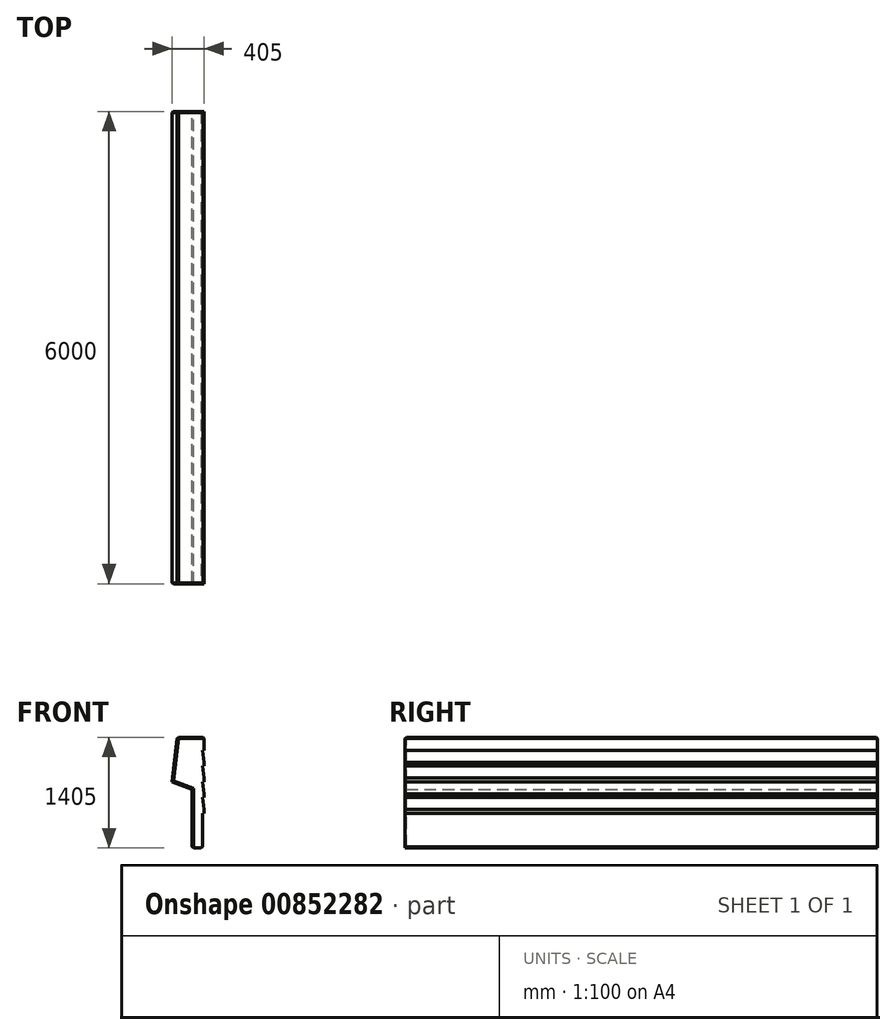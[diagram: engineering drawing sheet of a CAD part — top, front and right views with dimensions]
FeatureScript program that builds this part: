
annotation { "Feature Type Name" : "Feature", "Feature Type Description" : "" }
export const myFeature = defineFeature(function(context is Context, id is Id, definition is map)
    precondition{}
    {
        {
            assignVariable(context, id + "F0", {"name" : "BarrierLength", "anyValue" : 6000});
        }
        {
            var Q0;
            Q0=qCreatedBy(makeId("Front.planeOp"),FACE);
            var sketch = newSketch(context, id + "F1", { "sketchPlane" : qUnion([Q0])});
            skLineSegment(sketch, "E0", {"start": v(0, 0) * mm, "end": v(65, 565) * mm});
            skLineSegment(sketch, "E1", {"start": v(65, 565) * mm, "end": v(405, 565) * mm});
            skLineSegment(sketch, "E2", {"start": v(405, 565) * mm, "end": v(405, 400) * mm});
            skLineSegment(sketch, "E3", {"start": v(405, 400) * mm, "end": v(385, 400) * mm});
            skLineSegment(sketch, "E4", {"start": v(385, 400) * mm, "end": v(405, 250) * mm});
            skLineSegment(sketch, "E5", {"start": v(385, -400) * mm, "end": v(385, -840) * mm});
            skLineSegment(sketch, "E6", {"start": v(385, -840) * mm, "end": v(255, -840) * mm});
            skLineSegment(sketch, "E7", {"start": v(255, -840) * mm, "end": v(255, -95) * mm});
            skLineSegment(sketch, "E8", {"start": v(255, -95) * mm, "end": v(0, 0) * mm});
            skLineSegment(sketch, "E9", {"start": v(405, 250) * mm, "end": v(405, 200) * mm});
            skLineSegment(sketch, "E10", {"start": v(405, 200) * mm, "end": v(385, 200) * mm});
            skLineSegment(sketch, "E11", {"start": v(385, 200) * mm, "end": v(405, 50) * mm});
            skLineSegment(sketch, "E12", {"start": v(405, 50) * mm, "end": v(405, 0) * mm});
            skLineSegment(sketch, "E13", {"start": v(405, 0) * mm, "end": v(385, 0) * mm});
            skLineSegment(sketch, "E14", {"start": v(385, 0) * mm, "end": v(405, -150) * mm});
            skLineSegment(sketch, "E15", {"start": v(405, -150) * mm, "end": v(405, -200) * mm});
            skLineSegment(sketch, "E16", {"start": v(405, -200) * mm, "end": v(385, -200) * mm});
            skLineSegment(sketch, "E17", {"start": v(385, -200) * mm, "end": v(405, -350) * mm});
            skLineSegment(sketch, "E18", {"start": v(405, -350) * mm, "end": v(405, -400) * mm});
            skLineSegment(sketch, "E19", {"start": v(405, -400) * mm, "end": v(385, -400) * mm});
            skSolve(sketch);
        }
        {
            var Q0;
            Q0=makeQuery(id+"F1.imprint","IMPRINT",FACE,{"disambiguationData":[TD([[makeQuery(id+"F1.imprint","IMPRINT",EDGE,{"derivedFrom":sQuery(id+"F1.wireOp",EDGE,"E0")}),-1.0]])]});
            extrude(context, id + "F2", {"entities" : qUnion([Q0]), "depth" : (getVariable(context, 'BarrierLength')) * mm, "offsetDistance" : 25 * mm});
        }
        {
            var Q0;
            Q0=makeQuery(id+"F2.opExtrude","SWEPT_EDGE",EDGE,{"disambiguationData":[OSD([sQuery(id+"F1.wireOp",EDGE,"E0"),sQuery(id+"F1.wireOp",EDGE,"E1")])]});
            var Q1;
            Q1=makeQuery(id+"F2.opExtrude","SWEPT_EDGE",EDGE,{"disambiguationData":[OSD([sQuery(id+"F1.wireOp",EDGE,"E1"),sQuery(id+"F1.wireOp",EDGE,"E2")])]});
            var Q2;
            Q2=makeQuery(id+"F2.opExtrude","CAP_EDGE",EDGE,{"disambiguationData":[OSD([sQuery(id+"F1.wireOp",EDGE,"E1")])],"isStart":true});
            var Q3;
            Q3=makeQuery(id+"F2.opExtrude","CAP_EDGE",EDGE,{"disambiguationData":[OSD([sQuery(id+"F1.wireOp",EDGE,"E0")])],"isStart":true});
            var Q4;
            Q4=makeQuery(id+"F2.opExtrude","CAP_EDGE",EDGE,{"disambiguationData":[OSD([sQuery(id+"F1.wireOp",EDGE,"E1")])],"isStart":false});
            var Q5;
            Q5=makeQuery(id+"F2.opExtrude","CAP_EDGE",EDGE,{"disambiguationData":[OSD([sQuery(id+"F1.wireOp",EDGE,"E0")])],"isStart":false});
            var Q6;
            Q6=makeQuery(id+"F2.opExtrude","CAP_EDGE",EDGE,{"disambiguationData":[OSD([sQuery(id+"F1.wireOp",EDGE,"E8")])],"isStart":false});
            var Q7;
            Q7=makeQuery(id+"F2.opExtrude","CAP_EDGE",EDGE,{"disambiguationData":[OSD([sQuery(id+"F1.wireOp",EDGE,"E7")])],"isStart":false});
            var Q8;
            Q8=makeQuery(id+"F2.opExtrude","SWEPT_EDGE",EDGE,{"disambiguationData":[OSD([sQuery(id+"F1.wireOp",EDGE,"E5"),sQuery(id+"F1.wireOp",EDGE,"E6")])]});
            var Q9;
            Q9=makeQuery(id+"F2.opExtrude","SWEPT_EDGE",EDGE,{"disambiguationData":[OSD([sQuery(id+"F1.wireOp",EDGE,"E6"),sQuery(id+"F1.wireOp",EDGE,"E7")])]});
            var Q10;
            Q10=makeQuery(id+"F2.opExtrude","CAP_EDGE",EDGE,{"disambiguationData":[OSD([sQuery(id+"F1.wireOp",EDGE,"E7")])],"isStart":true});
            chamfer(context, id + "F3", {"entities" : qUnion([Q0, Q1, Q2, Q3, Q4, Q5, Q6, Q7, Q8, Q9, Q10]), "width" : 15 * mm, "tangentPropagation" : true});
        }
    });
